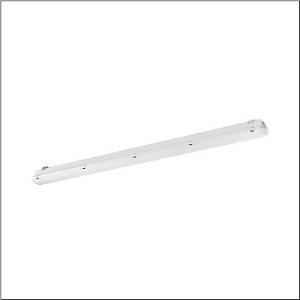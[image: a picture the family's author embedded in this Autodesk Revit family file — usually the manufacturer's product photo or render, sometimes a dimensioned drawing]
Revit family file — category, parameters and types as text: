
# Revit family: monsun_11xtreme_ho_51fe10dp480s
name_source: partatom
category: Lighting Fixtures
units: mm (PartAtom-declared; Revit-internal decimal feet)

## family parameters
Cut with Voids When Loaded = No
Host = Face
Light Source = No
Part Type = Normal
Room Calculation Point = No
Round Connector Dimension = Use Diameter
Shared = No

## types (1)
- --- (1 x LED, 8000 lm, 41 W, 4000K)
    Apparent Load = 41 VA
    CIE Flux Codes = 47 76 93 94 100
    Color Rendering = 80
    Color Temperature = 4000K
    Default Elevation = 1800 mm
    Description = Monsun 11Xtreme HO, damp-proof luminaire, chain hanger, primary optical cover: enclosure, of PMMA, light emission: direct distribution, primary light characteristic: symmetric, installation type: suspended mounting, surface-mounted, horizontal mounting, vertical mounting, LED, rated luminous flux: 8.000lm, luminous efficacy: 195lm/W, light colour: 840, colour temperature: 4000K, control gear: DALI 2, with terminal, 5-pole, max. 2.5mm², mains connection: 220..240V, AC, 50/60Hz, rated input power: 41W, luminaire housing, of glass-fibre reinforced polyester, uncoated, bright grey, incl. chain hanger, length: 1.590mm, width: 90mm, height: 88mm, clip for enclosure, of stainless steel (V2A), ceiling mounting element, of stainless steel (V2A), chain hanger, of stainless steel (V2A), protection rating (complete): IP66, insulation class (complete): insulation class I (protective earthing), certification: CE, ENEC, VDE, UKCA, protection symbol: D, impact resistance: IK04, permissible operating ambient temperature: -40..+45°C, standard: EN 50419, EN 60598-2-1, contact your sales advisor before using the luminaires in applications with unclear chemical exposure, large temperature fluctuations or condensation-forming humidity, LABS conformity tested according to VDMA 24364:2018-05, no direct snow, no direct sun, no direct rain, for indoor or canopied outdoor use, corresponds to IFS (International Featured Standards) requirements for safety and quality in the food industry, packaging unit: 1 piece
    Height = 88 mm
    Lamp = 1 x LED
    Lamp Light Flux = 8000 lm
    Lamp Power = 41 W
    Lamp count = 1
    Length = 1590 mm
    Luminous efficacy = 195 lm/W
    Manufacturer = Siteco
    ModVariant = No
    Model = 51FE10DP480S
    Mounting Place = Ceiling
    Mounting Type = Surface mounted
    Number of Poles = 1
    OnlyDefault = Yes
    Power Factor = 1
    Product Name = Monsun 11Xtreme HO
    Product group = damp-proof luminaire
    ProductGroupID = 300
    Protection Class = Protection class I
    Protection Degree = IP 66
    RLX_Detail_Level = 1
    RLX_Emergency_Light_Flux = 0 lm
    RLX_Emergency_Type = 0
    RLX_Emergency_Type_DB = No
    RlxData = <blob elided: 87593 chars, md5=eab48f66>
    Socket = socket
    Standby Power = 0 W
    System Light Flux = 8000 lm
    System Power = 41 W
    Type Comments = factory setting: luminous flux: 100 % | dim-lin: 254 | 284 mA
    Type Image = l_1349234.jpg
    URL = http://relux.com
    VarID = @adj_037891
    Voltage = 0 V
    Weight = 0.00 kg
    Width = 90 mm

## geometry (parser evidence)
native form markers: Blend x4, Sweep x13
no freeform markers — native parametric forms only
